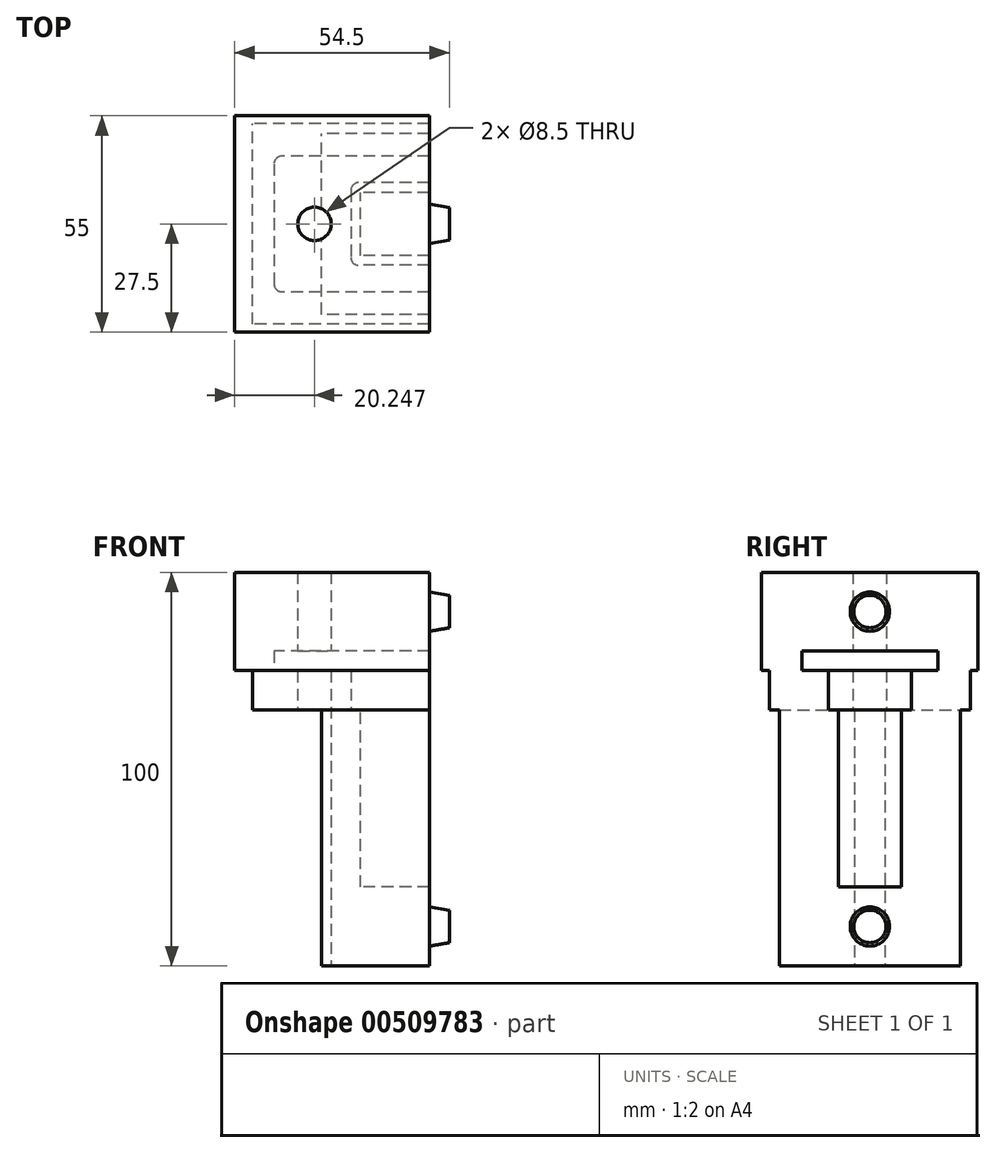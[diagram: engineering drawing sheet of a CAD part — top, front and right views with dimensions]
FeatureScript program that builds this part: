
annotation { "Feature Type Name" : "Feature", "Feature Type Description" : "" }
export const myFeature = defineFeature(function(context is Context, id is Id, definition is map)
    precondition{}
    {
        {
            var Q0;
            Q0=qCreatedBy(makeId("Top.planeOp"),FACE);
            var sketch = newSketch(context, id + "F0", { "sketchPlane" : qUnion([Q0])});
            skLineSegment(sketch, "E0.bottom", {"start": v(27.5, -23) * mm, "end": v(-27.5, -23) * mm});
            skLineSegment(sketch, "E0.top", {"start": v(27.5, 23) * mm, "end": v(-27.5, 23) * mm});
            skLineSegment(sketch, "E0.left", {"start": v(27.5, -23) * mm, "end": v(27.5, 23) * mm});
            skLineSegment(sketch, "E0.right", {"start": v(-27.5, -23) * mm, "end": v(-27.5, 23) * mm});
            skPoint(sketch, "E0.middle", {"position": v(0, 0) * mm});
            skSolve(sketch);
        }
        {
            var Q0;
            Q0=qSketchRegion(id+"F0",true);
            extrude(context, id + "F1", {"entities" : qUnion([Q0]), "depth" : 65 * mm});
        }
        {
            var Q0;
            Q0=makeQuery(id+"F1.opExtrude","CAP_FACE",FACE,{"disambiguationData":[OSD([sQuery(id+"F0.wireOp",EDGE,"E0.bottom"),sQuery(id+"F0.wireOp",EDGE,"E0.top"),sQuery(id+"F0.wireOp",EDGE,"E0.left"),sQuery(id+"F0.wireOp",EDGE,"E0.right")])],"isStart":false});
            var sketch = newSketch(context, id + "F2", { "sketchPlane" : qUnion([Q0])});
            skLineSegment(sketch, "E1.bottom", {"start": v(17.5, -8) * mm, "end": v(-17.5, -8) * mm});
            skLineSegment(sketch, "E1.top", {"start": v(17.5, 8) * mm, "end": v(-17.5, 8) * mm});
            skLineSegment(sketch, "E1.left", {"start": v(17.5, -8) * mm, "end": v(17.5, 8) * mm});
            skLineSegment(sketch, "E1.right", {"start": v(-17.5, -8) * mm, "end": v(-17.5, 8) * mm});
            skPoint(sketch, "E1.middle", {"position": v(0, 0) * mm});
            skSolve(sketch);
        }
        {
            var Q0;
            Q0=qSketchRegion(id+"F2",true);
            extrude(context, id + "F3", {"entities" : qUnion([Q0]), "operationType" : NewBodyOperationType.REMOVE, "oppositeDirection" : true, "depth" : 45 * mm});
        }
        {
            var Q0;
            Q0=makeQuery(id+"F1.opExtrude","CAP_FACE",FACE,{"disambiguationData":[OSD([sQuery(id+"F0.wireOp",EDGE,"E0.bottom"),sQuery(id+"F0.wireOp",EDGE,"E0.top"),sQuery(id+"F0.wireOp",EDGE,"E0.left"),sQuery(id+"F0.wireOp",EDGE,"E0.right")])],"isStart":false});
            var sketch = newSketch(context, id + "F4", { "sketchPlane" : qUnion([Q0])});
            skLineSegment(sketch, "E2.bottom", {"start": v(45, -25.5) * mm, "end": v(-45, -25.5) * mm});
            skLineSegment(sketch, "E2.top", {"start": v(45, 25.5) * mm, "end": v(-45, 25.5) * mm});
            skLineSegment(sketch, "E2.left", {"start": v(45, -25.5) * mm, "end": v(45, 25.5) * mm});
            skLineSegment(sketch, "E2.right", {"start": v(-45, -25.5) * mm, "end": v(-45, 25.5) * mm});
            skPoint(sketch, "E2.middle", {"position": v(0, 0) * mm});
            skSolve(sketch);
        }
        {
            var Q0;
            Q0=qSketchRegion(id+"F4",true);
            extrude(context, id + "F5", {"entities" : qUnion([Q0]), "operationType" : NewBodyOperationType.ADD, "depth" : 10 * mm});
        }
        {
            var Q0;
            {var subQ0=sQuery(id+"F4.wireOp",EDGE,"E2.right");var subQ1=sQuery(id+"F4.wireOp",EDGE,"E2.bottom");var subQ2=sQuery(id+"F4.wireOp",EDGE,"E2.top");var subQ3=sQuery(id+"F4.wireOp",EDGE,"E2.left");Q0=makeQuery(id+"F5.boolean.opBoolean","SPLIT",FACE,{"disambiguationData":[TD([makeQuery(id+"F1.opExtrude","SWEPT_FACE",FACE,{"disambiguationData":[OSD([sQuery(id+"F0.wireOp",EDGE,"E0.bottom")])]})])],"derivedFrom":makeQuery(id+"F5.opExtrude","CAP_FACE",FACE,{"disambiguationData":[OSD([subQ1,subQ2,subQ3,subQ0])],"isStart":true})});}
            var sketch = newSketch(context, id + "F6", { "sketchPlane" : qUnion([Q0])});
            skLineSegment(sketch, "E3.bottom", {"start": v(20, -10.5) * mm, "end": v(-20, -10.5) * mm});
            skLineSegment(sketch, "E3.top", {"start": v(20, 10.5) * mm, "end": v(-20, 10.5) * mm});
            skLineSegment(sketch, "E3.left", {"start": v(20, -10.5) * mm, "end": v(20, 10.5) * mm});
            skLineSegment(sketch, "E3.right", {"start": v(-20, -10.5) * mm, "end": v(-20, 10.5) * mm});
            skPoint(sketch, "E3.middle", {"position": v(0, 0) * mm});
            skSolve(sketch);
        }
        {
            var Q0;
            Q0=qSketchRegion(id+"F6",true);
            extrude(context, id + "F7", {"entities" : qUnion([Q0]), "operationType" : NewBodyOperationType.REMOVE, "oppositeDirection" : true, "depth" : 10 * mm});
        }
        {
            var Q0;
            Q0=makeQuery(id+"F7.boolean.opBoolean","COPY",EDGE,{"derivedFrom":makeQuery(id+"F7.opExtrude","SWEPT_EDGE",EDGE,{"disambiguationData":[OSD([sQuery(id+"F6.wireOp",EDGE,"E3.top"),sQuery(id+"F6.wireOp",EDGE,"E3.right")])]})});
            var Q1;
            Q1=makeQuery(id+"F7.boolean.opBoolean","COPY",EDGE,{"derivedFrom":makeQuery(id+"F7.opExtrude","SWEPT_EDGE",EDGE,{"disambiguationData":[OSD([sQuery(id+"F6.wireOp",EDGE,"E3.bottom"),sQuery(id+"F6.wireOp",EDGE,"E3.right")])]})});
            var Q2;
            Q2=makeQuery(id+"F7.boolean.opBoolean","COPY",EDGE,{"derivedFrom":makeQuery(id+"F7.opExtrude","SWEPT_EDGE",EDGE,{"disambiguationData":[OSD([sQuery(id+"F6.wireOp",EDGE,"E3.bottom"),sQuery(id+"F6.wireOp",EDGE,"E3.left")])]})});
            var Q3;
            Q3=makeQuery(id+"F7.boolean.opBoolean","COPY",EDGE,{"derivedFrom":makeQuery(id+"F7.opExtrude","SWEPT_EDGE",EDGE,{"disambiguationData":[OSD([sQuery(id+"F6.wireOp",EDGE,"E3.top"),sQuery(id+"F6.wireOp",EDGE,"E3.left")])]})});
            fillet(context, id + "F8", {"entities" : qUnion([Q0, Q1, Q2, Q3]), "radius" : 2 * mm, "tangentPropagation" : true, "allowEdgeOverflow" : false});
        }
        {
            var Q0;
            Q0=makeQuery(id+"F5.opExtrude","CAP_FACE",FACE,{"disambiguationData":[OSD([sQuery(id+"F4.wireOp",EDGE,"E2.bottom"),sQuery(id+"F4.wireOp",EDGE,"E2.top"),sQuery(id+"F4.wireOp",EDGE,"E2.left"),sQuery(id+"F4.wireOp",EDGE,"E2.right")])],"isStart":false});
            var sketch = newSketch(context, id + "F9", { "sketchPlane" : qUnion([Q0])});
            skLineSegment(sketch, "E4.bottom", {"start": v(49.5, -27.5) * mm, "end": v(-49.5, -27.5) * mm});
            skLineSegment(sketch, "E4.top", {"start": v(49.5, 27.5) * mm, "end": v(-49.5, 27.5) * mm});
            skLineSegment(sketch, "E4.left", {"start": v(49.5, -27.5) * mm, "end": v(49.5, 27.5) * mm});
            skLineSegment(sketch, "E4.right", {"start": v(-49.5, -27.5) * mm, "end": v(-49.5, 27.5) * mm});
            skPoint(sketch, "E4.middle", {"position": v(0, 0) * mm});
            skSolve(sketch);
        }
        {
            var Q0;
            Q0=qSketchRegion(id+"F9",true);
            extrude(context, id + "F10", {"entities" : qUnion([Q0]), "operationType" : NewBodyOperationType.ADD, "depth" : 25 * mm});
        }
        {
            var Q0;
            {var subQ0=sQuery(id+"F9.wireOp",EDGE,"E4.bottom");var subQ1=sQuery(id+"F9.wireOp",EDGE,"E4.top");var subQ2=sQuery(id+"F9.wireOp",EDGE,"E4.left");var subQ3=sQuery(id+"F9.wireOp",EDGE,"E4.right");Q0=makeQuery(id+"F10.boolean.opBoolean","SPLIT",FACE,{"disambiguationData":[TD([makeQuery(id+"F5.opExtrude","SWEPT_FACE",FACE,{"disambiguationData":[OSD([sQuery(id+"F4.wireOp",EDGE,"E2.bottom")])]})])],"derivedFrom":makeQuery(id+"F10.opExtrude","CAP_FACE",FACE,{"disambiguationData":[OSD([subQ0,subQ1,subQ2,subQ3])],"isStart":true})});}
            var sketch = newSketch(context, id + "F11", { "sketchPlane" : qUnion([Q0])});
            skLineSegment(sketch, "E5.bottom", {"start": v(39.5, -17.25) * mm, "end": v(-39.5, -17.25) * mm});
            skLineSegment(sketch, "E5.top", {"start": v(39.5, 17.25) * mm, "end": v(-39.5, 17.25) * mm});
            skLineSegment(sketch, "E5.left", {"start": v(39.5, -17.25) * mm, "end": v(39.5, 17.25) * mm});
            skLineSegment(sketch, "E5.right", {"start": v(-39.5, -17.25) * mm, "end": v(-39.5, 17.25) * mm});
            skPoint(sketch, "E5.middle", {"position": v(0, 0) * mm});
            skLineSegment(sketch, "E6.bottom", {"start": v(-27.93, -52.48) * mm, "end": v(-110.22, -52.48) * mm});
            skLineSegment(sketch, "E6.top", {"start": v(-27.93, -53.94) * mm, "end": v(-110.22, -53.94) * mm});
            skLineSegment(sketch, "E6.left", {"start": v(-27.93, -52.48) * mm, "end": v(-27.93, -53.94) * mm});
            skLineSegment(sketch, "E6.right", {"start": v(-110.22, -52.48) * mm, "end": v(-110.22, -53.94) * mm});
            skPoint(sketch, "E6.middle", {"position": v(-69.08, -53.2) * mm});
            skSolve(sketch);
        }
        {
            var Q0;
            Q0=qSketchRegion(id+"F11",true);
            extrude(context, id + "F12", {"entities" : qUnion([Q0]), "operationType" : NewBodyOperationType.REMOVE, "oppositeDirection" : true, "depth" : 5 * mm});
        }
        {
            var Q0;
            Q0=makeQuery(id+"F12.boolean.opBoolean","COPY",EDGE,{"derivedFrom":makeQuery(id+"F12.opExtrude","SWEPT_EDGE",EDGE,{"disambiguationData":[OSD([sQuery(id+"F11.wireOp",EDGE,"E5.bottom"),sQuery(id+"F11.wireOp",EDGE,"E5.right")])]})});
            fillet(context, id + "F13", {"entities" : qUnion([Q0]), "radius" : 2 * mm, "tangentPropagation" : true, "allowEdgeOverflow" : false});
        }
        {
            var Q0;
            Q0=makeQuery(id+"F12.boolean.opBoolean","COPY",EDGE,{"derivedFrom":makeQuery(id+"F12.opExtrude","SWEPT_EDGE",EDGE,{"disambiguationData":[OSD([sQuery(id+"F11.wireOp",EDGE,"E5.top"),sQuery(id+"F11.wireOp",EDGE,"E5.right")])]})});
            fillet(context, id + "F14", {"entities" : qUnion([Q0]), "radius" : 2 * mm, "tangentPropagation" : true, "allowEdgeOverflow" : false});
        }
        {
            var Q0;
            Q0=makeQuery(id+"F12.boolean.opBoolean","COPY",EDGE,{"derivedFrom":makeQuery(id+"F12.opExtrude","SWEPT_EDGE",EDGE,{"disambiguationData":[OSD([sQuery(id+"F11.wireOp",EDGE,"E5.top"),sQuery(id+"F11.wireOp",EDGE,"E5.left")])]})});
            fillet(context, id + "F15", {"entities" : qUnion([Q0]), "radius" : 2 * mm, "tangentPropagation" : true, "allowEdgeOverflow" : false});
        }
        {
            var Q0;
            Q0=makeQuery(id+"F12.boolean.opBoolean","COPY",EDGE,{"derivedFrom":makeQuery(id+"F12.opExtrude","SWEPT_EDGE",EDGE,{"disambiguationData":[OSD([sQuery(id+"F11.wireOp",EDGE,"E5.bottom"),sQuery(id+"F11.wireOp",EDGE,"E5.left")])]})});
            fillet(context, id + "F16", {"entities" : qUnion([Q0]), "radius" : 2 * mm, "tangentPropagation" : true, "allowEdgeOverflow" : false});
        }
        {
            var Q0;
            Q0=makeQuery(id+"F12.boolean.opBoolean","COPY",FACE,{"derivedFrom":makeQuery(id+"F12.opExtrude","CAP_FACE",FACE,{"disambiguationData":[OSD([sQuery(id+"F11.wireOp",EDGE,"E5.bottom"),sQuery(id+"F11.wireOp",EDGE,"E5.top"),sQuery(id+"F11.wireOp",EDGE,"E5.left"),sQuery(id+"F11.wireOp",EDGE,"E5.right")])],"isStart":false})});
            var sketch = newSketch(context, id + "F17", { "sketchPlane" : qUnion([Q0])});
            skLineSegment(sketch, "E7", {"start": v(-39.25, -0.06) * mm, "end": v(-29.25, 0) * mm});
            skCircle(sketch, "E8", {"center": v(-29.25, 0) * mm, "radius": 4.25 * mm});
            skSolve(sketch);
        }
        {
            var Q0;
            Q0=qSketchRegion(id+"F17",true);
            extrude(context, id + "F18", {"entities" : qUnion([Q0]), "operationType" : NewBodyOperationType.REMOVE, "endBound" : BoundingType.SYMMETRIC, "oppositeDirection" : true, "depth" : 200 * mm});
        }
        {
            var Q0;
            Q0=makeQuery(id+"F12.boolean.opBoolean","COPY",FACE,{"derivedFrom":makeQuery(id+"F12.opExtrude","CAP_FACE",FACE,{"disambiguationData":[OSD([sQuery(id+"F11.wireOp",EDGE,"E5.bottom"),sQuery(id+"F11.wireOp",EDGE,"E5.top"),sQuery(id+"F11.wireOp",EDGE,"E5.left"),sQuery(id+"F11.wireOp",EDGE,"E5.right")])],"isStart":false})});
            var sketch = newSketch(context, id + "F19", { "sketchPlane" : qUnion([Q0])});
            skLineSegment(sketch, "E9", {"start": v(39.5, 0) * mm, "end": v(29.5, 0) * mm});
            skPoint(sketch, "E9.endSnap0", {"position": v(39.5, 0) * mm});
            skCircle(sketch, "E10", {"center": v(29.5, 0) * mm, "radius": 4.25 * mm});
            skSolve(sketch);
        }
        {
            var Q0;
            Q0=qSketchRegion(id+"F19",true);
            extrude(context, id + "F20", {"entities" : qUnion([Q0]), "operationType" : NewBodyOperationType.ADD, "depth" : 5 * mm});
        }
        {
            var Q0;
            Q0=qCreatedBy(makeId("Right.planeOp"),FACE);
            var sketch = newSketch(context, id + "F21", { "sketchPlane" : qUnion([Q0])});
            skLineSegment(sketch, "E11.bottom", {"start": v(-77.03, 103.08) * mm, "end": v(67.56, 103.08) * mm});
            skLineSegment(sketch, "E11.top", {"start": v(-77.03, -60.44) * mm, "end": v(67.56, -60.44) * mm});
            skLineSegment(sketch, "E11.left", {"start": v(-77.03, 103.08) * mm, "end": v(-77.03, -60.44) * mm});
            skLineSegment(sketch, "E11.right", {"start": v(67.56, 103.08) * mm, "end": v(67.56, -60.44) * mm});
            skSolve(sketch);
        }
        {
            var Q0;
            Q0=makeQuery(id+"F21.imprint","IMPRINT",FACE,{"disambiguationData":[TD([[makeQuery(id+"F21.imprint","IMPRINT",EDGE,{"derivedFrom":sQuery(id+"F21.wireOp",EDGE,"E11.bottom")}),-1.0]])]});
            var Q1;
            Q1=makeQuery(id+"F10.opExtrude","SWEPT_FACE",FACE,{"disambiguationData":[OSD([sQuery(id+"F9.wireOp",EDGE,"E4.left")])]});
            var Q2;
            Q2=makeQuery(id+"F1.opExtrude","SWEPT_FACE",FACE,{"disambiguationData":[OSD([sQuery(id+"F0.wireOp",EDGE,"E0.left")])]});
            extrude(context, id + "F22", {"entities" : qUnion([Q0, Q1, Q2]), "operationType" : NewBodyOperationType.REMOVE, "endBound" : BoundingType.THROUGH_ALL, "depth" : 25 * mm});
        }
        {
            var Q0;
            Q0=makeQuery(id+"F22.boolean.opBoolean","COPY",FACE,{"derivedFrom":makeQuery(id+"F22.opExtrude","CAP_FACE",FACE,{"disambiguationData":[OSD([sQuery(id+"F21.wireOp",EDGE,"E11.bottom"),sQuery(id+"F21.wireOp",EDGE,"E11.top"),sQuery(id+"F21.wireOp",EDGE,"E11.left"),sQuery(id+"F21.wireOp",EDGE,"E11.right")])],"isStart":true})});
            var sketch = newSketch(context, id + "F23", { "sketchPlane" : qUnion([Q0])});
            skCircle(sketch, "E12", {"center": v(0, 10) * mm, "radius": 5 * mm});
            skCircle(sketch, "E13", {"center": v(0, 90) * mm, "radius": 5 * mm});
            skPoint(sketch, "E13.centerSnap0", {"position": v(0, 100) * mm});
            skSolve(sketch);
        }
        {
            var Q0;
            Q0=qSketchRegion(id+"F23",true);
            extrude(context, id + "F24", {"entities" : qUnion([Q0]), "operationType" : NewBodyOperationType.ADD, "depth" : 5 * mm, "hasDraft" : true, "draftAngle" : 10 * degree, "draftPullDirection" : true});
        }
    });
